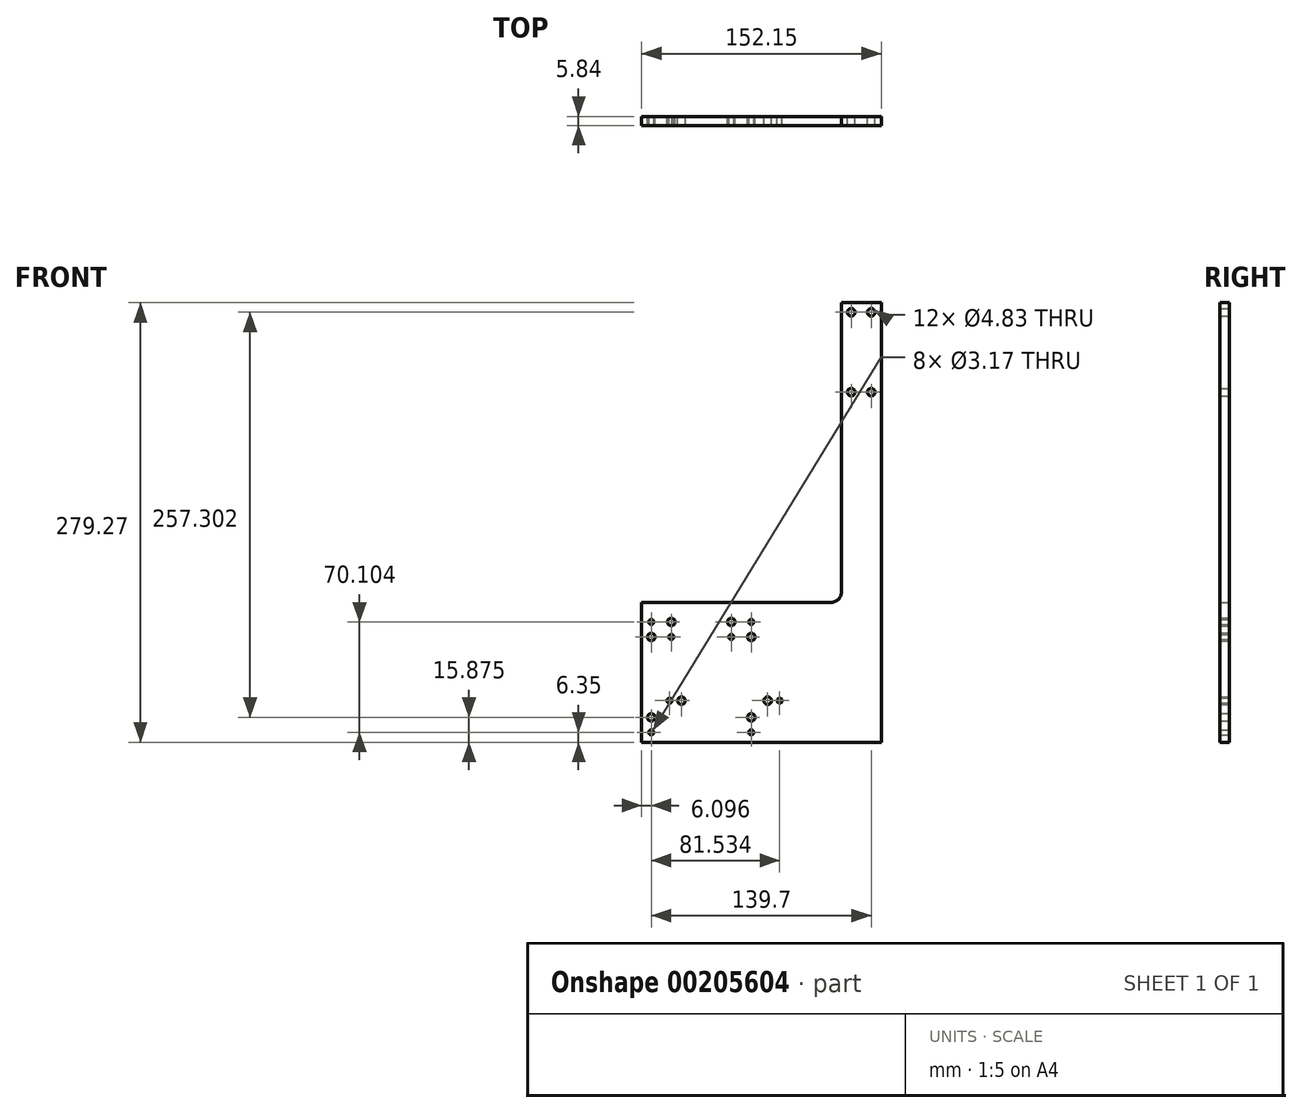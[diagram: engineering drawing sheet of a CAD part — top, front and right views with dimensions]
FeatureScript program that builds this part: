
annotation { "Feature Type Name" : "Feature", "Feature Type Description" : "" }
export const myFeature = defineFeature(function(context is Context, id is Id, definition is map)
    precondition{}
    {
        {
            var Q0;
            Q0=qCreatedBy(makeId("Front.planeOp"),FACE);
            var sketch = newSketch(context, id + "F0", { "sketchPlane" : qUnion([Q0])});
            skLineSegment(sketch, "E0", {"start": v(0, 0) * mm, "end": v(126.75, 0) * mm});
            skLineSegment(sketch, "E1", {"start": v(126.75, 0) * mm, "end": v(126.75, 190.37) * mm});
            skLineSegment(sketch, "E2", {"start": v(126.75, 190.37) * mm, "end": v(152.15, 190.37) * mm});
            skLineSegment(sketch, "E3", {"start": v(152.15, 190.37) * mm, "end": v(152.15, -88.9) * mm});
            skLineSegment(sketch, "E4", {"start": v(152.15, -88.9) * mm, "end": v(0, -88.9) * mm});
            skLineSegment(sketch, "E5", {"start": v(0, -88.9) * mm, "end": v(0, 0) * mm});
            skCircle(sketch, "E6", {"center": v(18.8, -12.45) * mm, "radius": 2.41 * mm});
            skCircle(sketch, "E7", {"center": v(56.9, -12.45) * mm, "radius": 2.41 * mm});
            skCircle(sketch, "E8", {"center": v(18.8, -21.97) * mm, "radius": 1.59 * mm});
            skCircle(sketch, "E9", {"center": v(56.9, -21.97) * mm, "radius": 1.59 * mm});
            skCircle(sketch, "E10", {"center": v(69.6, -12.45) * mm, "radius": 1.59 * mm});
            skCircle(sketch, "E11", {"center": v(69.6, -21.97) * mm, "radius": 2.41 * mm});
            skCircle(sketch, "E12", {"center": v(6.1, -12.45) * mm, "radius": 1.59 * mm});
            skCircle(sketch, "E13", {"center": v(6.1, -21.97) * mm, "radius": 2.41 * mm});
            skCircle(sketch, "E14", {"center": v(6.1, -73.03) * mm, "radius": 2.41 * mm});
            skCircle(sketch, "E15", {"center": v(6.1, -82.55) * mm, "radius": 1.59 * mm});
            skCircle(sketch, "E16", {"center": v(69.6, -73.03) * mm, "radius": 2.41 * mm});
            skCircle(sketch, "E17", {"center": v(69.6, -82.55) * mm, "radius": 1.59 * mm});
            skCircle(sketch, "E18", {"center": v(133.1, 184.28) * mm, "radius": 2.41 * mm});
            skCircle(sketch, "E19", {"center": v(145.8, 184.28) * mm, "radius": 2.41 * mm});
            skCircle(sketch, "E20", {"center": v(133.1, 133.53) * mm, "radius": 2.41 * mm});
            skCircle(sketch, "E21", {"center": v(145.8, 133.53) * mm, "radius": 2.41 * mm});
            skCircle(sketch, "E22", {"center": v(17.63, -62.4) * mm, "radius": 1.59 * mm});
            skCircle(sketch, "E23", {"center": v(25.25, -62.4) * mm, "radius": 2.41 * mm});
            skCircle(sketch, "E24", {"center": v(80.01, -62.4) * mm, "radius": 2.41 * mm});
            skCircle(sketch, "E25", {"center": v(87.63, -62.4) * mm, "radius": 1.59 * mm});
            skSolve(sketch);
        }
        {
            var Q0;
            Q0=qSketchRegion(id+"F0",true);
            extrude(context, id + "F1", {"entities" : qUnion([Q0]), "depth" : 5.84 * mm});
        }
        {
            var Q0;
            Q0=makeQuery(id+"F1.opExtrude","SWEPT_EDGE",EDGE,{"disambiguationData":[OSD([sQuery(id+"F0.wireOp",EDGE,"E0"),sQuery(id+"F0.wireOp",EDGE,"E1")])]});
            fillet(context, id + "F2", {"entities" : qUnion([Q0]), "radius" : 6.35 * mm, "tangentPropagation" : true, "allowEdgeOverflow" : false});
        }
    });
